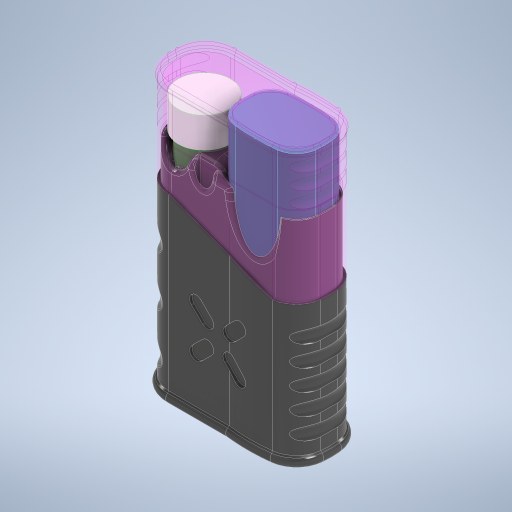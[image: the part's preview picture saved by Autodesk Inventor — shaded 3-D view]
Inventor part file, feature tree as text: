
AUTODESK INVENTOR PART (.ipt)
format: ipt  version: 2023 (Build 270158030, 158C)  size: 3,500,544 bytes
history: native  units: mm
features: fillet x27, sketch x27, extrude x23, projected_geometry x17, other x6, revolve x5, pattern_circular x2, plane x1, sweep x1, mirror x1
ambient origin geometry x8: Origin, YZ Plane, XZ Plane, XY Plane, X Axis, Y Axis, Z Axis, Center Point
bodies: Body1 (feature_tree), Body2 (feature_tree), Body3 (feature_tree), Body4 (feature_tree)
feature tree (110):
  other  "vape"
  extrude  "Extrusion1"  Depth=8.35mm
  fillet  "Fillet1"  Radius=80.0mm
  extrude  "Extrusion2"  Depth=11.6mm TaperAngle=0.0deg
  plane  "Work Plane1"
  extrude  "Extrusion3"  Depth=45.8mm TaperAngle=0.0deg
  extrude  "Extrusion4"  Depth=22.1mm
  extrude  "Extrusion5"  Depth=1.5mm
  extrude  "Extrusion6"  Depth=1.5mm
  fillet  "Fillet2"  Radius=1.5mm
  extrude  "Extrusion8"  Depth=15.55mm
  extrude  "Extrusion20"  Depth=3.0mm
  extrude  "Extrusion21"  Depth=3.0mm
  sweep  "Sweep2"
  sketch  "Sketch26"  dims[d105=71.0mm d106=0.0mm d108=71.0mm d109=0.0mm d110=3.0mm d111=30.0deg]
  extrude  "Extrusion22"  Depth=13.0mm
  fillet  "Fillet22"  Radius=2.0mm
  fillet  "Fillet23"  Radius=10.0mm
  fillet  "Fillet24"  Radius=11.0mm
  fillet  "Fillet25"  Radius=4.0mm
  fillet  "Fillet26"  Radius=2.0mm
  fillet  "Fillet4"  Radius=3.0mm
  extrude  "Extrusion10"  Depth=2.4mm
  extrude  "Extrusion11"  Depth=7.0mm
  fillet  "Fillet10"  Radius=45.0mm
  fillet  "Fillet27"  Radius=0.25mm
  extrude  "Extrusion13"  Depth=71.0mm TaperAngle=0.0deg
  fillet  "Fillet28"  Radius=3.0mm
  sketch  "Sketch14"  dims[d50=3.0mm d51=3.0mm]
  extrude  "Extrusion14"  Depth=15.0mm TaperAngle=0.0deg
  extrude  "Extrusion23"  TaperAngle=0.0deg  [1 undecoded]
  extrude  "Extrusion24"  Depth=15.0mm
  extrude  "Extrusion15"  Depth=20.0mm
  fillet  "Fillet29"  Radius=9.0mm
  extrude  "Extrusion25"  Depth=6.0mm
  fillet  "Fillet30"  Radius=4.0mm
  other  "Work Axis1"
  revolve  "Revolution1"  [1 undecoded]
  sketch  "Sketch30"  dims[d172=15.780931mm d173=20.0mm d174=9.0mm]
  revolve  "Revolution2"  [1 undecoded]
  fillet  "Fillet32"  Radius=1.0mm
  extrude  "Extrusion26"  Depth=2.5mm
  sketch  "Sketch35"  dims[d178=1.0mm d179=2.0mm]
  revolve  "Revolution3"  [1 undecoded]
  revolve  "Revolution5"  [1 undecoded]
  extrude  "Extrusion27"  Depth=10.0mm TaperAngle=0.0deg
  extrude  "Extrusion28"  Depth=6.0mm
  fillet  "Fillet34"  Radius=3.65mm
  other  "Work Axis2"
  revolve  "Revolution6"  [1 undecoded]
  pattern_circular  "Circular Pattern1"  [2 undecoded]
  extrude  "Extrusion29"  Depth=14.0mm
  fillet  "Fillet35"  Radius=19.0mm
  fillet  "Fillet36"  [1 undecoded]
  fillet  "Fillet37"  Radius=8.0mm
  fillet  "Fillet38"  Radius=8.0mm
  fillet  "Fillet39"  Radius=8.0mm
  fillet  "Fillet40"  Radius=8.0mm
  fillet  "Fillet41"  Radius=8.0mm
  pattern_circular  "Circular Pattern2"  [2 undecoded]
  fillet  "Fillet42"  [1 undecoded]
  fillet  "Fillet43"  [1 undecoded]
  fillet  "Fillet44"  Radius=1.5mm
  fillet  "Fillet45"  Radius=0.5mm
  fillet  "Fillet46"  Radius=18.25mm
  extrude  "Extrusion30"  Depth=8.0mm
  mirror  "Mirror1"
  sketch  "Sketch1"  dims[d4=98.5mm d5=0.0mm d9=8.35mm d22=80.0mm d23=0.0mm]
  sketch  "Sketch2"  dims[d24=20.0mm d26=11.6mm d27=0.0mm]
  other  "vape-tube"
  sketch  "Sketch3"  dims[d28=17.0mm d29=45.8mm d30=0.0mm]
  other  "storage"
  sketch  "Sketch4"  dims[d31=17.0mm d38=22.1mm]
  sketch  "Sketch5"  dims[d39=31.1mm d41=1.5mm]
  projected_geometry  "Projected Loop2"
  sketch  "Sketch6"  dims[d42=1.5mm d44=1.5mm d45=1.5mm]
  projected_geometry  "Projected Loop3"
  projected_geometry  "Projected Loop4"
  sketch  "Sketch8"  dims[d46=11.05mm d47=15.55mm]
  projected_geometry  "Projected Loop6"
  sketch  "Sketch11"  dims[d48=3.0mm d49=3.0mm]
  sketch  "Sketch15"  dims[d52=11.05mm d53=15.55mm]
  other  "vape-lid"
  sketch  "Sketch22"  dims[d54=2.0mm d55=13.0mm]
  projected_geometry  "Projected Loop13"
  sketch  "Sketch23"  dims[d56=12.5mm d57=60.0mm d58=0.0mm d59=2.0mm d60=10.0mm d61=0.0mm d62=11.0mm d66=4.0mm d67=8.726646mm d69=2.0mm d83=3.0mm]
  projected_geometry  "Projected Loop14"
  sketch  "Sketch24"  dims[d86=72.0mm d87=0.0mm d88=2.4mm]
  sketch  "Sketch25"  dims[d89=7.3mm d91=7.0mm d92=45.0mm d93=0.0mm d94=0.25mm]
  sketch  "Sketch27"  dims[d158=1.0mm d159=15.0mm d160=0.0mm]
  projected_geometry  "Projected Loop15"
  projected_geometry  "Projected Loop16"
  projected_geometry  "Projected Loop17"
  projected_geometry  "Projected Loop18"
  projected_geometry  "Projected Loop19"
  projected_geometry  "Projected Loop20"
  sketch  "Sketch28"  dims[d161=15.0mm d162=0.0mm d163=0.0mm d164=0.0mm]
  sketch  "Sketch29"  dims[d169=0.0mm d170=0.0mm d171=15.0mm]
  sketch  "Sketch33"  dims[d175=7.5mm d176=6.0mm d177=4.0mm]
  projected_geometry  "Projected Loop31"
  sketch  "Sketch37"  dims[d180=1.2mm d181=0.5mm d182=1.0mm]
  sketch  "Sketch38"  dims[d183=24.0mm d184=2.5mm]
  projected_geometry  "Projected Loop32"
  sketch  "Sketch39"  dims[d185=0.7mm d186=2.35mm]
  projected_geometry  "Projected Loop33"
  projected_geometry  "Projected Loop34"
  projected_geometry  "Projected Loop35"
  sketch  "Sketch40"  dims[d187=4.0mm d188=0.5mm]
  sketch  "Sketch41"  dims[d189=10.0mm d190=0.0mm d191=10.0mm d192=0.0mm]
  sketch  "Sketch44"  dims[d193=1.5mm d194=6.0mm d195=3.65mm d196=10.0mm d197=0.0mm d198=2.5mm d199=14.0mm d200=19.0mm d201=19.0mm d207=180.0deg d208=8.0mm d209=8.0mm d210=8.0mm d211=8.0mm d212=8.0mm d213=12.5mm d215=0.0mm d216=180.0deg d218=1.5mm d220=0.5mm d221=18.25mm d222=0.0mm d223=8.0mm d224=7.0mm d225=6.0mm d226=6.0mm d227=11.5mm d228=6.0mm d229=6.0mm d230=180.0deg d240=3.0mm d241=6.0mm d242=6.0mm d243=6.0mm d244=41.5mm d245=11.5mm d246=6.0mm d247=180.0deg d249=20.0mm d253=22.0mm d254=22.0mm d255=25.0mm d256=1.0mm d257=1.0mm d258=0.0mm d259=1.0mm d260=0.0mm d261=0.2mm d262=11.0mm d263=5.0mm d264=10.0mm d265=2.241222mm d266=10.0mm d267=30.0mm d268=4.0mm d269=45.0deg d270=40.0mm d271=360.0deg d275=0.4mm d276=1.1mm d277=2.4mm d278=3.0mm d279=1.5mm d280=3.0mm d281=0.810487mm d282=2.943591mm d283=4.5mm d284=0.0mm d285=2.0mm d286=0.8mm d287=3.0mm d288=0.5mm d289=1.0mm d290=1.0mm d291=1.0mm d292=40.0mm d293=360.0deg d295=1.0mm d296=0.5mm d297=0.5mm d298=1.0mm d299=0.4mm d309=59.760104mm d310=29.880052mm d311=30.0mm d312=12.0mm d313=45.0deg d315=8.5mm d316=8.5mm d317=5.0mm d318=40.0mm d320=360.0deg d322=10.0mm d323=1.0mm d324=0.0mm d325=0.0mm]
note: 13 required parameter values undecoded (feature->parameter linkage not recoverable at this tier; creation-order binding heuristic only, values carry confidence <= 0.55)